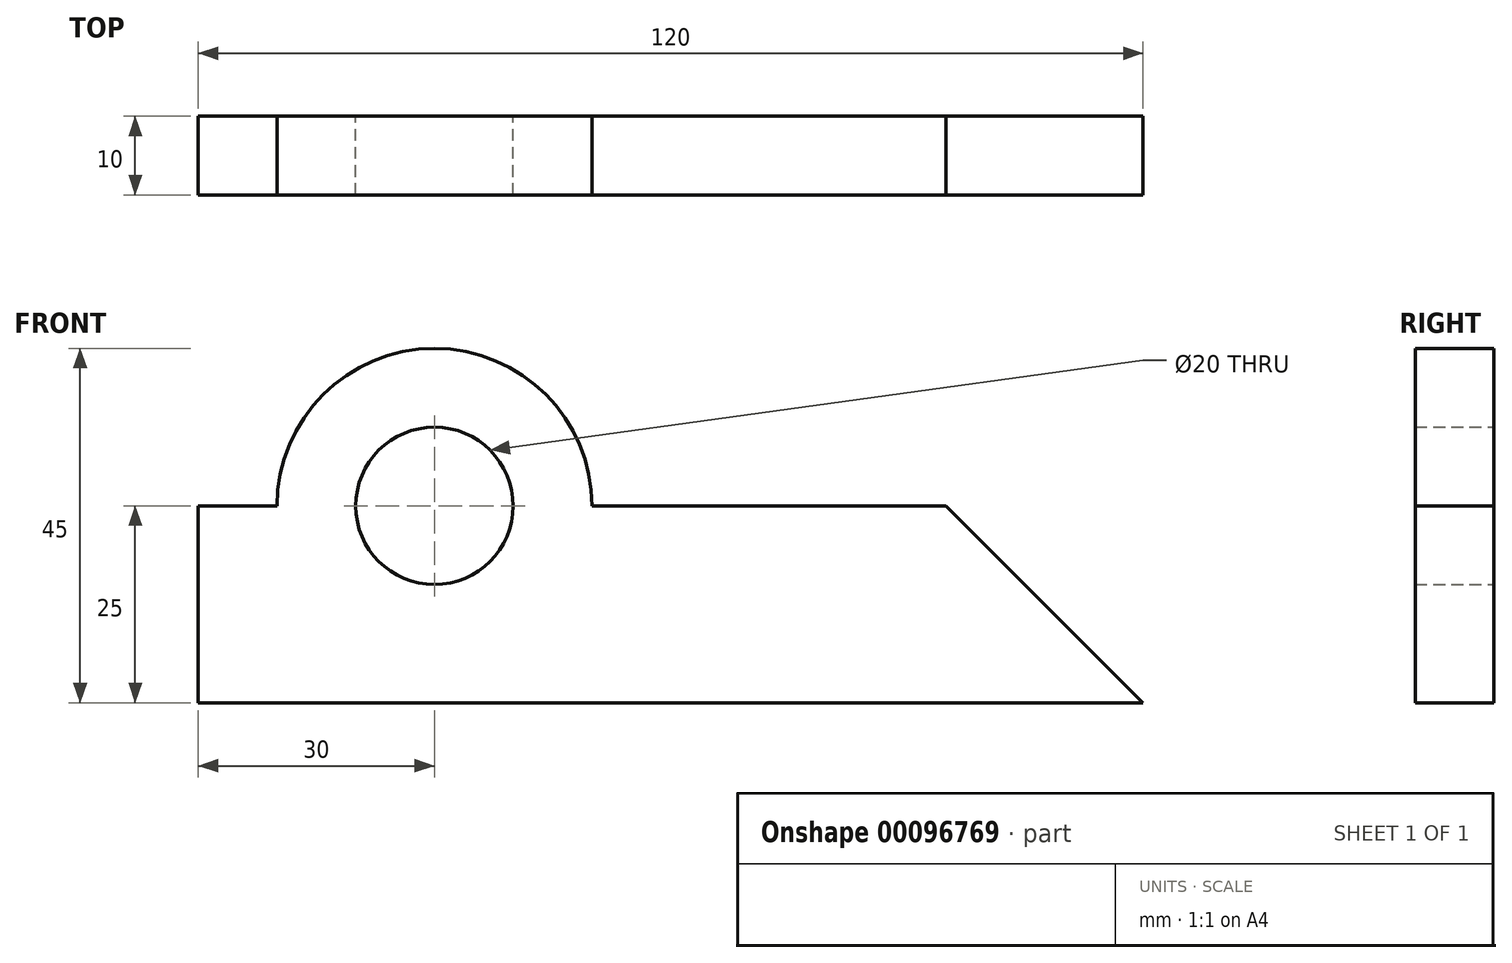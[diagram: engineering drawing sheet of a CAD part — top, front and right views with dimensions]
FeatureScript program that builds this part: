
annotation { "Feature Type Name" : "Feature", "Feature Type Description" : "" }
export const myFeature = defineFeature(function(context is Context, id is Id, definition is map)
    precondition{}
    {
        {
            var Q0;
            Q0=qCreatedBy(makeId("Front.planeOp"),FACE);
            var sketch = newSketch(context, id + "F0", { "sketchPlane" : qUnion([Q0])});
            skLineSegment(sketch, "E0", {"start": v(0, 0) * mm, "end": v(0, 25) * mm});
            skLineSegment(sketch, "E1", {"start": v(95, 25) * mm, "end": v(120, 0) * mm});
            skLineSegment(sketch, "E2", {"start": v(120, 0) * mm, "end": v(0, 0) * mm});
            skLineSegment(sketch, "E3", {"start": v(0, 25) * mm, "end": v(10, 25) * mm});
            skLineSegment(sketch, "E4", {"start": v(95, 25) * mm, "end": v(50, 25) * mm});
            skArc(sketch, "E5", {"start": v(50, 25) * mm, "mid": v(30, 45) * mm, "end": v(10, 25) * mm});
            skCircle(sketch, "E6", {"center": v(30, 25) * mm, "radius": 10 * mm});
            skLineSegment(sketch, "E7", {"start": v(10, 25) * mm, "end": v(50, 25) * mm, "construction": true});
            skSolve(sketch);
        }
        {
            var Q0;
            Q0 = qSketchRegion(id + "F0", true);
            extrude(context, id + "F1", {"entities" : qUnion([Q0]), "depth" : 10 * mm});
        }
    });
